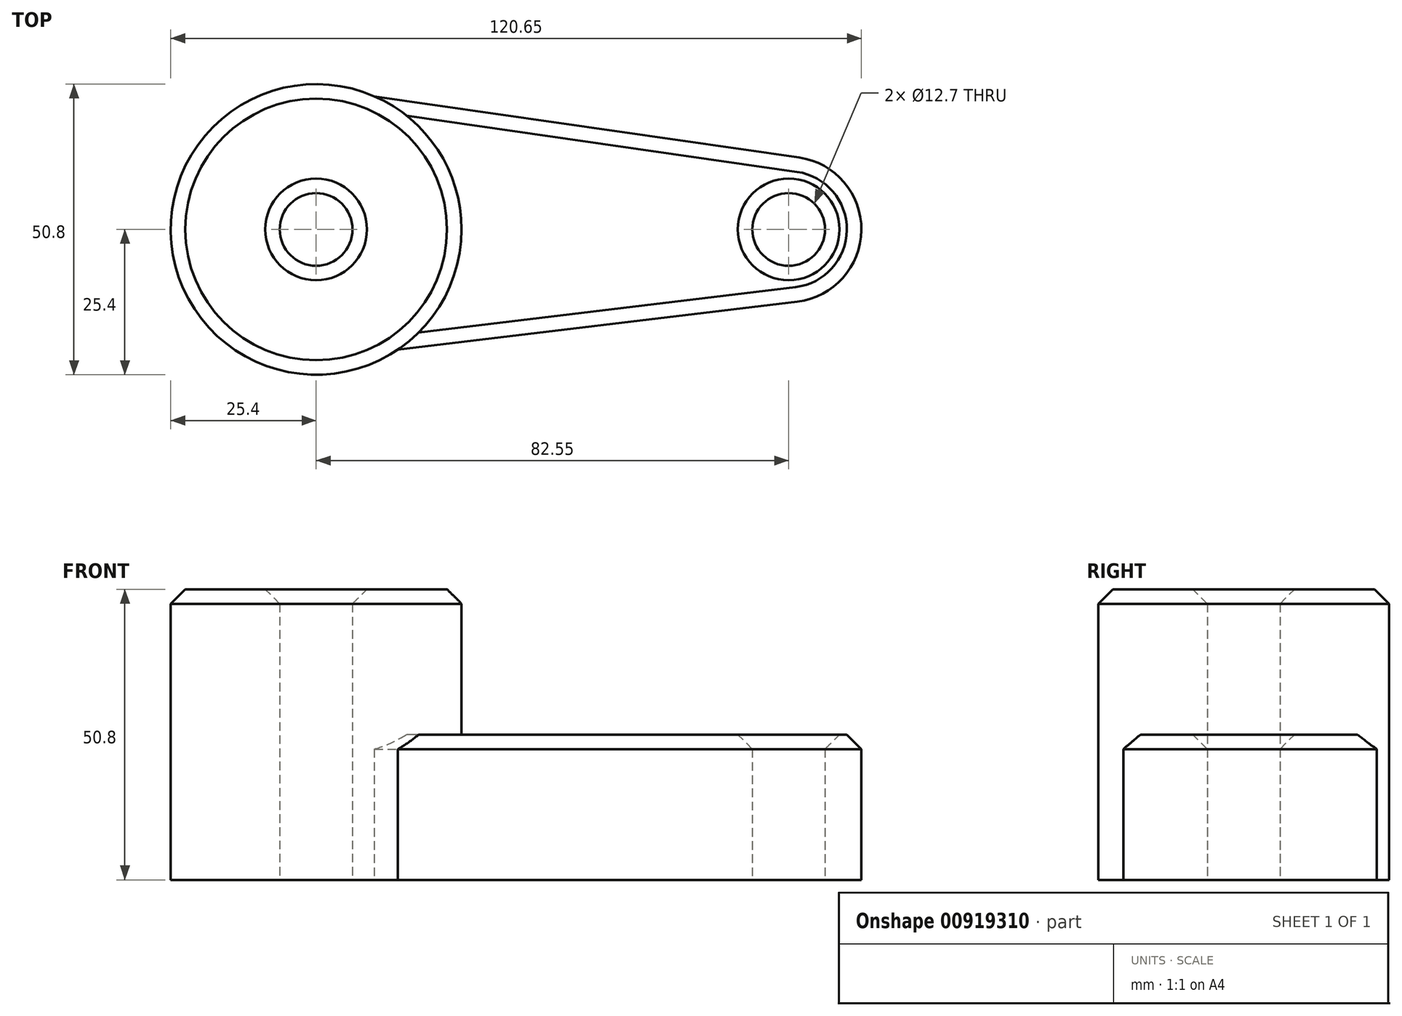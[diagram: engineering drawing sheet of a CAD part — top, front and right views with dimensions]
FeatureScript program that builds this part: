
annotation { "Feature Type Name" : "Feature", "Feature Type Description" : "" }
export const myFeature = defineFeature(function(context is Context, id is Id, definition is map)
    precondition{}
    {
        {
            var Q0;
            Q0=qCreatedBy(makeId("Top.planeOp"),FACE);
            var sketch = newSketch(context, id + "F0", { "sketchPlane" : qUnion([Q0])});
            skCircle(sketch, "E0", {"center": v(0, 0) * mm, "radius": 25.4 * mm});
            skCircle(sketch, "E1", {"center": v(82.55, 0) * mm, "radius": 12.7 * mm});
            skLineSegment(sketch, "E2", {"start": v(14.27, -21.01) * mm, "end": v(84.07, -12.6) * mm});
            skLineSegment(sketch, "E3", {"start": v(10.17, 23.28) * mm, "end": v(84.36, 12.57) * mm});
            skCircle(sketch, "E4", {"center": v(0, 0) * mm, "radius": 6.35 * mm});
            skCircle(sketch, "E5", {"center": v(82.55, 0) * mm, "radius": 6.35 * mm});
            skSolve(sketch);
        }
        {
            var Q0;
            Q0=makeQuery(id+"F0.imprint","IMPRINT",FACE,{"disambiguationData":[TD([[makeQuery(id+"F0.imprint","IMPRINT",EDGE,{"derivedFrom":sQuery(id+"F0.wireOp",EDGE,"E4")}),-1.0]])]});
            var Q1;
            Q1=makeQuery(id+"F0.imprint","IMPRINT",FACE,{"disambiguationData":[TD([[makeQuery(id+"F0.imprint","IMPRINT",EDGE,{"derivedFrom":sQuery(id+"F0.wireOp",EDGE,"E5")}),-1.0]])]});
            var Q2;
            {var subQ0=sQuery(id+"F0.wireOp",EDGE,"E2");Q2=makeQuery(id+"F0.imprint","IMPRINT",FACE,{"disambiguationData":[TD([[makeQuery(id+"F0.imprint","IMPRINT",EDGE,{"derivedFrom":subQ0}),1.0]])]});}
            extrude(context, id + "F1", {"entities" : qUnion([Q0, Q1, Q2]), "depth" : 25.4 * mm, "offsetDistance" : 25.4 * mm});
        }
        {
            var Q0;
            Q0=makeQuery(id+"F0.imprint","IMPRINT",FACE,{"disambiguationData":[TD([[makeQuery(id+"F0.imprint","IMPRINT",EDGE,{"derivedFrom":sQuery(id+"F0.wireOp",EDGE,"E4")}),-1.0]])]});
            extrude(context, id + "F2", {"entities" : qUnion([Q0]), "operationType" : NewBodyOperationType.ADD, "depth" : 50.8 * mm, "offsetDistance" : 25.4 * mm});
        }
        {
            var Q0;
            Q0=makeQuery(id+"F2.opExtrude","CAP_EDGE",EDGE,{"disambiguationData":[OSD([sQuery(id+"F0.wireOp",EDGE,"E0")])],"isStart":false});
            var Q1;
            Q1=makeQuery(id+"F1.opExtrude","CAP_EDGE",EDGE,{"disambiguationData":[OSD([sQuery(id+"F0.wireOp",EDGE,"E1")])],"isStart":false});
            var Q2;
            Q2=makeQuery(id+"F1.opExtrude","CAP_EDGE",EDGE,{"disambiguationData":[OSD([sQuery(id+"F0.wireOp",EDGE,"E5")])],"isStart":false});
            var Q3;
            Q3=makeQuery(id+"F1.opExtrude","CAP_EDGE",EDGE,{"disambiguationData":[OSD([sQuery(id+"F0.wireOp",EDGE,"E2")])],"isStart":false});
            var Q4;
            Q4=makeQuery(id+"F2.opExtrude","CAP_EDGE",EDGE,{"disambiguationData":[OSD([sQuery(id+"F0.wireOp",EDGE,"E4")])],"isStart":false});
            var Q5;
            Q5=makeQuery(id+"F1.opExtrude","CAP_EDGE",EDGE,{"disambiguationData":[OSD([sQuery(id+"F0.wireOp",EDGE,"E3")])],"isStart":false});
            chamfer(context, id + "F3", {"entities" : qUnion([Q0, Q1, Q2, Q3, Q4, Q5]), "width" : 2.54 * mm, "tangentPropagation" : true});
        }
    });
